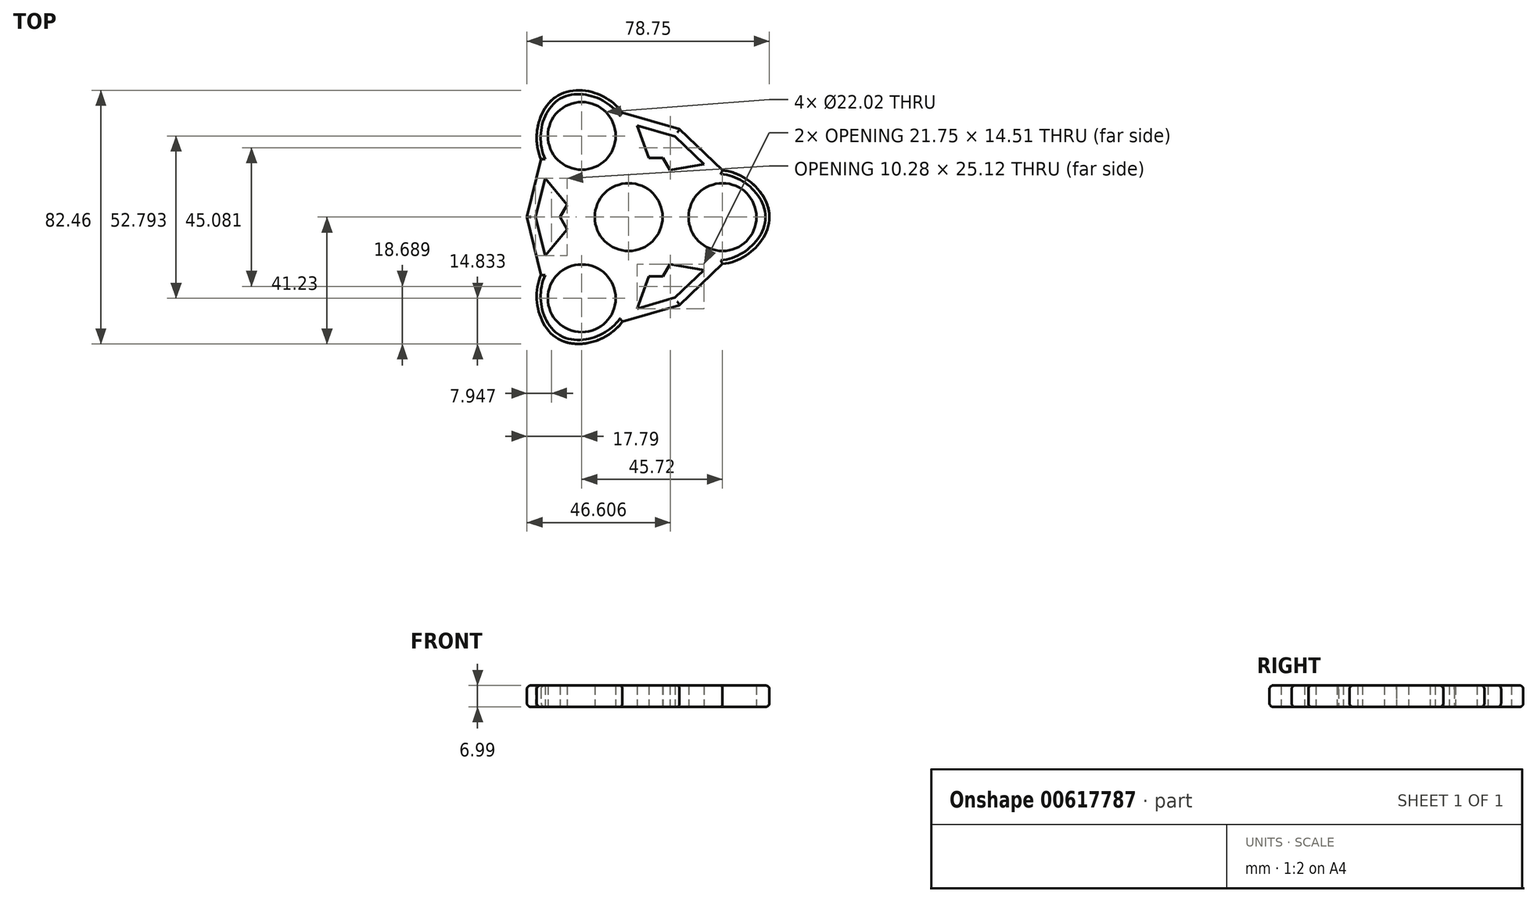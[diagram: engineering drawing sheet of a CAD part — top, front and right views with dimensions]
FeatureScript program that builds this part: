
annotation { "Feature Type Name" : "Feature", "Feature Type Description" : "" }
export const myFeature = defineFeature(function(context is Context, id is Id, definition is map)
    precondition{}
    {
        {
            var Q0;
            Q0=qCreatedBy(makeId("Top.planeOp"),FACE);
            var sketch = newSketch(context, id + "F0", { "sketchPlane" : qUnion([Q0])});
            skCircle(sketch, "E0", {"center": v(0, 0) * mm, "radius": 11.01 * mm});
            skCircle(sketch, "E1", {"center": v(30.48, 0) * mm, "radius": 11.01 * mm});
            skCircle(sketch, "E2", {"center": v(-15.24, 26.4) * mm, "radius": 11.01 * mm});
            skCircle(sketch, "E3", {"center": v(-15.24, -26.4) * mm, "radius": 11.01 * mm});
            skFitSpline(sketch, "E4", {"points": [v(-15.24, 0) * mm, v(-28.44, 18.78) * mm, v(-22.86, 39.6) * mm, v(-2.04, 34.02) * mm, v(7.62, 13.2) * mm, v(30.48, 15.24) * mm, v(45.72, 0) * mm, v(30.48, -15.24) * mm, v(7.62, -13.2) * mm, v(-2.04, -34.02) * mm, v(-22.86, -39.6) * mm, v(-28.44, -18.78) * mm, v(-15.24, 0) * mm]});
            skLineSegment(sketch, "E5", {"start": v(-28.44, 18.78) * mm, "end": v(-33.03, 0) * mm});
            skLineSegment(sketch, "E6", {"start": v(-33.03, 0) * mm, "end": v(-28.44, -18.78) * mm});
            skLineSegment(sketch, "E7", {"start": v(-2.04, -34.02) * mm, "end": v(16.51, -28.6) * mm});
            skLineSegment(sketch, "E8", {"start": v(16.51, -28.6) * mm, "end": v(30.48, -15.24) * mm});
            skLineSegment(sketch, "E9", {"start": v(30.48, 15.24) * mm, "end": v(16.51, 28.6) * mm});
            skLineSegment(sketch, "E10", {"start": v(16.51, 28.6) * mm, "end": v(-2.04, 34.02) * mm});
            skLineSegment(sketch, "E11.0", {"start": v(-27.15, 12.56) * mm, "end": v(-19.94, 3.97) * mm});
            skLineSegment(sketch, "E11.1", {"start": v(-19.94, 3.97) * mm, "end": v(-22.23, 0) * mm});
            skLineSegment(sketch, "E11.2", {"start": v(-22.23, 0) * mm, "end": v(-19.94, -3.97) * mm});
            skLineSegment(sketch, "E11.3", {"start": v(-19.94, -3.97) * mm, "end": v(-27.15, -12.56) * mm});
            skLineSegment(sketch, "E11.4", {"start": v(-27.15, -12.56) * mm, "end": v(-30.22, 0) * mm});
            skLineSegment(sketch, "E11.5", {"start": v(-30.22, 0) * mm, "end": v(-27.15, 12.56) * mm});
            skLineSegment(sketch, "E12.1.0", {"start": v(6.54, -19.26) * mm, "end": v(11.12, -19.26) * mm});
            skLineSegment(sketch, "E12.1.1", {"start": v(13.4, -15.29) * mm, "end": v(24.45, -17.24) * mm});
            skLineSegment(sketch, "E12.1.2", {"start": v(11.12, -19.26) * mm, "end": v(13.4, -15.29) * mm});
            skLineSegment(sketch, "E12.1.3", {"start": v(24.45, -17.24) * mm, "end": v(15.11, -26.17) * mm});
            skLineSegment(sketch, "E12.1.4", {"start": v(15.11, -26.17) * mm, "end": v(2.7, -29.8) * mm});
            skLineSegment(sketch, "E12.1.5", {"start": v(2.7, -29.8) * mm, "end": v(6.54, -19.26) * mm});
            skLineSegment(sketch, "E12.2.0", {"start": v(13.4, 15.29) * mm, "end": v(11.12, 19.26) * mm});
            skLineSegment(sketch, "E12.2.1", {"start": v(6.54, 19.26) * mm, "end": v(2.7, 29.8) * mm});
            skLineSegment(sketch, "E12.2.2", {"start": v(11.12, 19.26) * mm, "end": v(6.54, 19.26) * mm});
            skLineSegment(sketch, "E12.2.3", {"start": v(2.7, 29.8) * mm, "end": v(15.11, 26.17) * mm});
            skLineSegment(sketch, "E12.2.4", {"start": v(15.11, 26.17) * mm, "end": v(24.45, 17.24) * mm});
            skLineSegment(sketch, "E12.2.5", {"start": v(24.45, 17.24) * mm, "end": v(13.4, 15.29) * mm});
            skLineSegment(sketch, "E13", {"start": v(0, 0) * mm, "end": v(-15.24, -26.4) * mm});
            skLineSegment(sketch, "E14", {"start": v(0, 0) * mm, "end": v(30.48, 0) * mm});
            skLineSegment(sketch, "E15", {"start": v(-15.24, 26.4) * mm, "end": v(0, 0) * mm});
            skLineSegment(sketch, "E16", {"start": v(0, 0) * mm, "end": v(16.51, 28.6) * mm});
            skLineSegment(sketch, "E17", {"start": v(0, 0) * mm, "end": v(16.51, -28.6) * mm});
            skLineSegment(sketch, "E18", {"start": v(0, 0) * mm, "end": v(-33.03, 0) * mm});
            skLineSegment(sketch, "E19", {"start": v(-22.86, -39.6) * mm, "end": v(-15.24, -26.4) * mm});
            skLineSegment(sketch, "E20", {"start": v(30.48, 0) * mm, "end": v(45.72, 0) * mm});
            skLineSegment(sketch, "E21", {"start": v(-15.24, 26.4) * mm, "end": v(-22.86, 39.6) * mm});
            skLineSegment(sketch, "E22", {"start": v(-28.44, 18.78) * mm, "end": v(-2.04, 34.02) * mm});
            skLineSegment(sketch, "E23", {"start": v(-28.44, -18.78) * mm, "end": v(-2.04, -34.02) * mm});
            skLineSegment(sketch, "E24", {"start": v(30.48, 15.24) * mm, "end": v(30.48, -15.24) * mm});
            skSolve(sketch);
        }
        {
            var Q0;
            Q0 = qSketchRegion(id + "F0", true);
            extrude(context, id + "F1", {"entities" : qUnion([Q0]), "depth" : 7 * mm, "offsetDistance" : 25.4 * mm});
        }
        {
            var Q0;
            {var subQ1=sQuery(id+"F0.wireOp",EDGE,"E4");var subQ2=makeQuery(id+"F0.imprint","INTERSECT",VERTEX,{"derivedFrom":[subQ1,sQuery(id+"F0.wireOp",EDGE,"E21")]});Q0=makeQuery(id+"F1.opExtrude","CAP_EDGE",EDGE,{"disambiguationData":[OSD([subQ1]),TDD([makeQuery(id+"F0.imprint","IMPRINT",EDGE,{"disambiguationData":[TD([[subQ2,1.0]])],"derivedFrom":subQ1}),makeQuery(id+"F0.imprint","IMPRINT",EDGE,{"disambiguationData":[TD([[subQ2,-1.0]])],"derivedFrom":subQ1})])],"isStart":false});}
            var Q1;
            {var subQ1=sQuery(id+"F0.wireOp",EDGE,"E4");var subQ2=makeQuery(id+"F0.imprint","INTERSECT",VERTEX,{"derivedFrom":[subQ1,sQuery(id+"F0.wireOp",EDGE,"E20")]});Q1=makeQuery(id+"F1.opExtrude","CAP_EDGE",EDGE,{"disambiguationData":[OSD([subQ1]),TDD([makeQuery(id+"F0.imprint","IMPRINT",EDGE,{"disambiguationData":[TD([[subQ2,1.0]])],"derivedFrom":subQ1}),makeQuery(id+"F0.imprint","IMPRINT",EDGE,{"disambiguationData":[TD([[subQ2,-1.0]])],"derivedFrom":subQ1})])],"isStart":false});}
            var Q2;
            {var subQ1=sQuery(id+"F0.wireOp",EDGE,"E4");var subQ2=makeQuery(id+"F0.imprint","INTERSECT",VERTEX,{"derivedFrom":[subQ1,sQuery(id+"F0.wireOp",EDGE,"E19")]});Q2=makeQuery(id+"F1.opExtrude","CAP_EDGE",EDGE,{"disambiguationData":[OSD([subQ1]),TDD([makeQuery(id+"F0.imprint","IMPRINT",EDGE,{"disambiguationData":[TD([[subQ2,1.0]])],"derivedFrom":subQ1}),makeQuery(id+"F0.imprint","IMPRINT",EDGE,{"disambiguationData":[TD([[subQ2,-1.0]])],"derivedFrom":subQ1})])],"isStart":false});}
            var Q3;
            Q3=makeQuery(id+"F1.opExtrude","CAP_EDGE",EDGE,{"disambiguationData":[OSD([sQuery(id+"F0.wireOp",EDGE,"E7")])],"isStart":false});
            var Q4;
            Q4=makeQuery(id+"F1.opExtrude","CAP_EDGE",EDGE,{"disambiguationData":[OSD([sQuery(id+"F0.wireOp",EDGE,"E8")])],"isStart":false});
            var Q5;
            Q5=makeQuery(id+"F1.opExtrude","CAP_EDGE",EDGE,{"disambiguationData":[OSD([sQuery(id+"F0.wireOp",EDGE,"E9")])],"isStart":false});
            var Q6;
            Q6=makeQuery(id+"F1.opExtrude","CAP_EDGE",EDGE,{"disambiguationData":[OSD([sQuery(id+"F0.wireOp",EDGE,"E10")])],"isStart":false});
            var Q7;
            Q7=makeQuery(id+"F1.opExtrude","CAP_EDGE",EDGE,{"disambiguationData":[OSD([sQuery(id+"F0.wireOp",EDGE,"E5")])],"isStart":false});
            var Q8;
            Q8=makeQuery(id+"F1.opExtrude","CAP_EDGE",EDGE,{"disambiguationData":[OSD([sQuery(id+"F0.wireOp",EDGE,"E6")])],"isStart":false});
            fillet(context, id + "F2", {"entities" : qUnion([Q0, Q1, Q2, Q3, Q4, Q5, Q6, Q7, Q8]), "radius" : 1.27 * mm, "tangentPropagation" : true, "allowEdgeOverflow" : false});
        }
        {
            var Q0;
            Q0=makeQuery(id+"F1.opExtrude","CAP_EDGE",EDGE,{"disambiguationData":[OSD([sQuery(id+"F0.wireOp",EDGE,"E10")])],"isStart":true});
            var Q1;
            {var subQ1=sQuery(id+"F0.wireOp",EDGE,"E4");var subQ2=makeQuery(id+"F0.imprint","INTERSECT",VERTEX,{"derivedFrom":[subQ1,sQuery(id+"F0.wireOp",EDGE,"E21")]});Q1=makeQuery(id+"F1.opExtrude","CAP_EDGE",EDGE,{"disambiguationData":[OSD([subQ1]),TDD([makeQuery(id+"F0.imprint","IMPRINT",EDGE,{"disambiguationData":[TD([[subQ2,1.0]])],"derivedFrom":subQ1}),makeQuery(id+"F0.imprint","IMPRINT",EDGE,{"disambiguationData":[TD([[subQ2,-1.0]])],"derivedFrom":subQ1})])],"isStart":true});}
            var Q2;
            Q2=makeQuery(id+"F1.opExtrude","CAP_EDGE",EDGE,{"disambiguationData":[OSD([sQuery(id+"F0.wireOp",EDGE,"E5")])],"isStart":true});
            var Q3;
            Q3=makeQuery(id+"F1.opExtrude","CAP_EDGE",EDGE,{"disambiguationData":[OSD([sQuery(id+"F0.wireOp",EDGE,"E6")])],"isStart":true});
            var Q4;
            {var subQ1=sQuery(id+"F0.wireOp",EDGE,"E4");var subQ2=makeQuery(id+"F0.imprint","INTERSECT",VERTEX,{"derivedFrom":[subQ1,sQuery(id+"F0.wireOp",EDGE,"E19")]});Q4=makeQuery(id+"F1.opExtrude","CAP_EDGE",EDGE,{"disambiguationData":[OSD([subQ1]),TDD([makeQuery(id+"F0.imprint","IMPRINT",EDGE,{"disambiguationData":[TD([[subQ2,1.0]])],"derivedFrom":subQ1}),makeQuery(id+"F0.imprint","IMPRINT",EDGE,{"disambiguationData":[TD([[subQ2,-1.0]])],"derivedFrom":subQ1})])],"isStart":true});}
            var Q5;
            Q5=makeQuery(id+"F1.opExtrude","CAP_EDGE",EDGE,{"disambiguationData":[OSD([sQuery(id+"F0.wireOp",EDGE,"E7")])],"isStart":true});
            var Q6;
            Q6=makeQuery(id+"F1.opExtrude","CAP_EDGE",EDGE,{"disambiguationData":[OSD([sQuery(id+"F0.wireOp",EDGE,"E8")])],"isStart":true});
            var Q7;
            {var subQ1=sQuery(id+"F0.wireOp",EDGE,"E4");var subQ2=makeQuery(id+"F0.imprint","INTERSECT",VERTEX,{"derivedFrom":[subQ1,sQuery(id+"F0.wireOp",EDGE,"E20")]});Q7=makeQuery(id+"F1.opExtrude","CAP_EDGE",EDGE,{"disambiguationData":[OSD([subQ1]),TDD([makeQuery(id+"F0.imprint","IMPRINT",EDGE,{"disambiguationData":[TD([[subQ2,1.0]])],"derivedFrom":subQ1}),makeQuery(id+"F0.imprint","IMPRINT",EDGE,{"disambiguationData":[TD([[subQ2,-1.0]])],"derivedFrom":subQ1})])],"isStart":true});}
            var Q8;
            Q8=makeQuery(id+"F1.opExtrude","CAP_EDGE",EDGE,{"disambiguationData":[OSD([sQuery(id+"F0.wireOp",EDGE,"E9")])],"isStart":true});
            fillet(context, id + "F3", {"entities" : qUnion([Q0, Q1, Q2, Q3, Q4, Q5, Q6, Q7, Q8]), "radius" : 1.27 * mm, "tangentPropagation" : true, "allowEdgeOverflow" : false});
        }
    });
